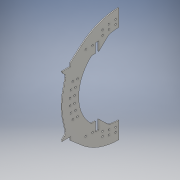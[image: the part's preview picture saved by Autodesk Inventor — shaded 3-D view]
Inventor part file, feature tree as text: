
AUTODESK INVENTOR PART (.ipt)
format: ipt  version: 2016 (Build 200138000, 138)  size: 470,528 bytes
history: native  units: in
note: dims shown in document units (in); Inventor stores cm internally (conversion verified against a paired STEP export)
features: reference x13, sketch x11, extrude x9, projected_geometry x4, hole x2, mirror x2, fillet x2, plane x1
ambient origin geometry x8: Origin, YZ Plane, XZ Plane, XY Plane, X Axis, Y Axis, Z Axis, Center Point
bodies: Solid1 (feature_tree)
feature tree (44):
  sketch  "Sketch1"  dims[d0=16.0in d2=12.0in]
  extrude  "Extrusion1"  Depth=12.0in
  hole  "Hole1"  [1 undecoded]
  extrude  "Extrusion2"  Depth=1.0in
  extrude  "Extrusion3"  Depth=0.5in
  extrude  "Extrusion5"  Depth=1.0in
  extrude  "Extrusion6"  TaperAngle=45.0deg  [1 undecoded]
  hole  "Hole4"  [1 undecoded]
  extrude  "Extrusion10"  Depth=0.125in TaperAngle=0.0deg
  extrude  "Extrusion11"  Depth=0.5in
  extrude  "Extrusion12"  Depth=0.5in
  plane  "Work Plane1"
  mirror  "Mirror1"
  fillet  "Fillet1"  Radius=0.5in
  extrude  "Extrusion13"  Depth=0.125in TaperAngle=0.0deg
  mirror  "Mirror2"
  fillet  "Fillet2"  Radius=1.0in
  sketch  "Sketch15"  dims[d32=0.125in d33=0.0in d34=0.5in d35=0.5in d36=0.125in d37=0.0in d56=0.26in d57=0.75in d58=0.375in d59=0.25in d60=0.5635in d61=1.0in d62=0.8108in d65=1.0in d66=0.0in d67=0.8712in d68=1.5in d71=1.5in d72=0.3212in d74=0.321in d75=0.125in d76=0.0in d78=0.5in d79=0.5in d81=1.5in d83=0.125in d84=0.0in d85=0.5in d86=0.125in d87=0.0in d88=0.5in]
  sketch  "Sketch2"  dims[d3=14.6in d5=2.0in]
  sketch  "Sketch3"  dims[d6=1.0in d7=1.0in]
  projected_geometry  "Projected Loop1"
  sketch  "Sketch4"  dims[d8=0.5in d9=0.5in]
  sketch  "Sketch5"  dims[d10=1.0in d11=1.0in]
  sketch  "Sketch9"  dims[d12=45.0deg d13=45.0deg]
  reference  "Reference11"
  reference  "Reference12"
  reference  "Reference13"
  reference  "Reference14"
  reference  "Reference15"
  sketch  "Sketch11"  dims[d14=0.25in d15=0.0in]
  reference  "Reference19"
  reference  "Reference20"
  reference  "Reference21"
  reference  "Reference22"
  sketch  "Sketch12"  dims[d16=0.26in d17=0.75in d18=0.375in d19=0.25in d20=0.5635in d21=1.0in d22=0.8108in d23=17.0in]
  projected_geometry  "Projected Loop4"
  reference  "Reference23"
  reference  "Reference24"
  reference  "Reference25"
  sketch  "Sketch13"  dims[d24=0.25in d25=0.0in d26=0.125in d27=0.0in]
  projected_geometry  "Projected Loop5"
  sketch  "Sketch14"  dims[d28=4.5in d29=0.5in]
  projected_geometry  "Projected Loop6"
  reference  "Reference26"
note: 3 required parameter values undecoded (feature->parameter linkage not recoverable at this tier; creation-order binding heuristic only, values carry confidence <= 0.55)
